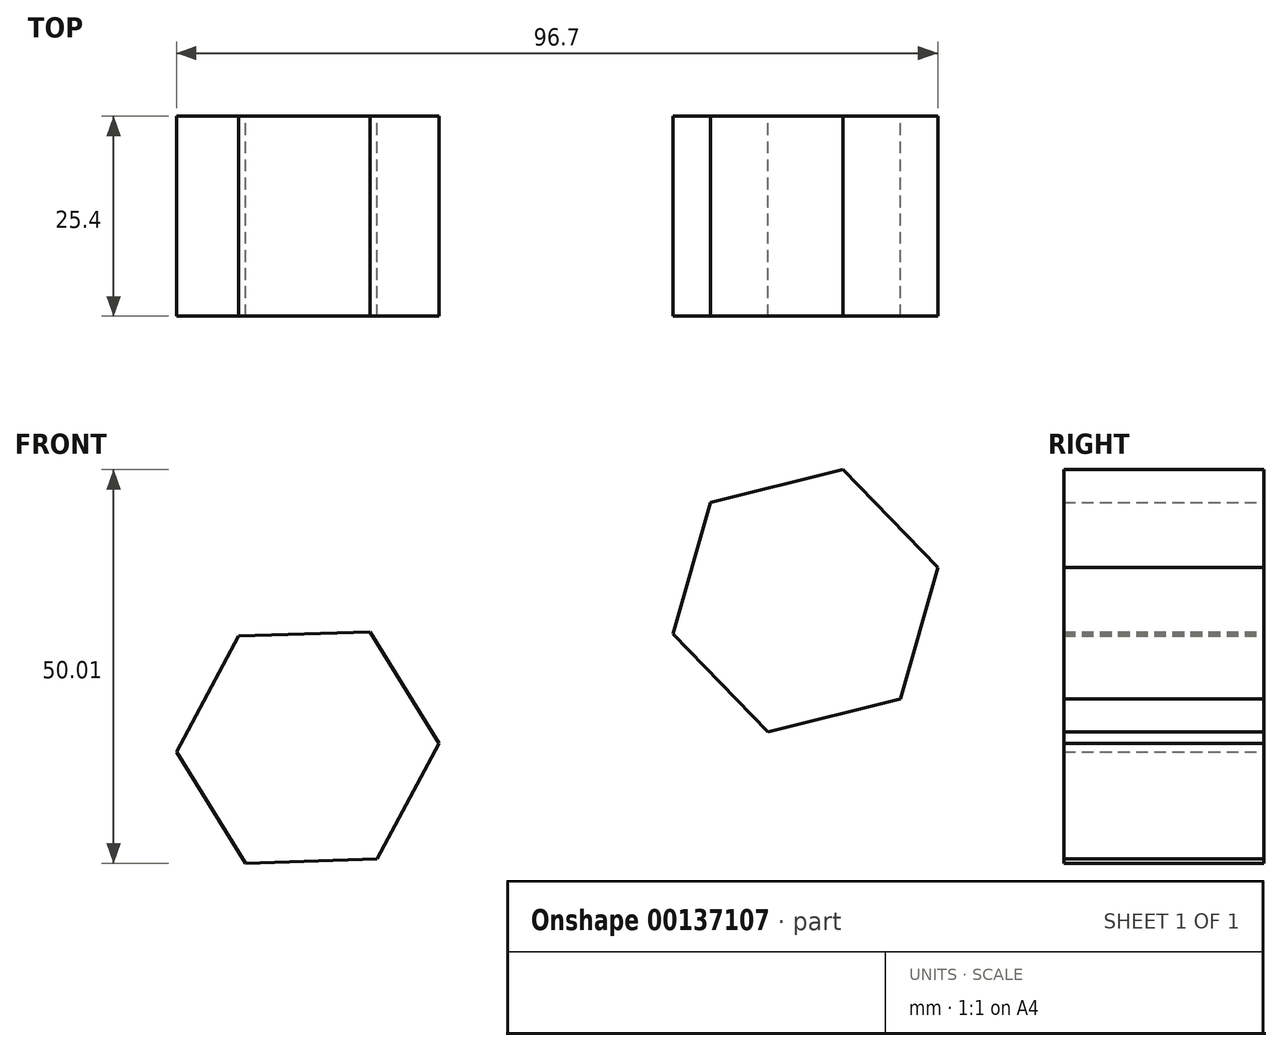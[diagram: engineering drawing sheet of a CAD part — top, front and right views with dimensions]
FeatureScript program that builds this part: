
annotation { "Feature Type Name" : "Feature", "Feature Type Description" : "" }
export const myFeature = defineFeature(function(context is Context, id is Id, definition is map)
    precondition{}
    {
        {
            var Q0;
            Q0=qCreatedBy(makeId("Front.planeOp"),FACE);
            var sketch = newSketch(context, id + "F0", { "sketchPlane" : qUnion([Q0])});
            skCircle(sketch, "E0.cCircle", {"center": v(-30.47, 21.15) * mm, "radius": 14.45 * mm, "construction": true});
            skLineSegment(sketch, "E0.0", {"start": v(-13.8, 21.68) * mm, "end": v(-21.68, 6.97) * mm});
            skLineSegment(sketch, "E0.1", {"start": v(-21.68, 6.97) * mm, "end": v(-38.35, 6.44) * mm});
            skLineSegment(sketch, "E0.2", {"start": v(-38.35, 6.44) * mm, "end": v(-47.15, 20.62) * mm});
            skLineSegment(sketch, "E0.3", {"start": v(-47.15, 20.62) * mm, "end": v(-39.27, 35.32) * mm});
            skLineSegment(sketch, "E0.4", {"start": v(-39.27, 35.32) * mm, "end": v(-22.6, 35.85) * mm});
            skLineSegment(sketch, "E0.5", {"start": v(-22.6, 35.85) * mm, "end": v(-13.8, 21.68) * mm});
            skPoint(sketch, "E0.0.midPoint", {"position": v(-17.74, 14.33) * mm});
            skCircle(sketch, "E1.cCircle", {"center": v(32.75, 39.8) * mm, "radius": 15 * mm, "construction": true});
            skLineSegment(sketch, "E1.0", {"start": v(44.79, 27.34) * mm, "end": v(27.98, 23.14) * mm});
            skLineSegment(sketch, "E1.1", {"start": v(27.98, 23.14) * mm, "end": v(15.94, 35.6) * mm});
            skLineSegment(sketch, "E1.2", {"start": v(15.94, 35.6) * mm, "end": v(20.7, 52.25) * mm});
            skLineSegment(sketch, "E1.3", {"start": v(20.7, 52.25) * mm, "end": v(37.51, 56.45) * mm});
            skLineSegment(sketch, "E1.4", {"start": v(37.51, 56.45) * mm, "end": v(49.55, 44) * mm});
            skLineSegment(sketch, "E1.5", {"start": v(49.55, 44) * mm, "end": v(44.79, 27.34) * mm});
            skPoint(sketch, "E1.0.midPoint", {"position": v(36.39, 25.24) * mm});
            skSolve(sketch);
        }
        {
            var Q0;
            Q0=makeQuery(id+"F0.imprint","IMPRINT",FACE,{"disambiguationData":[TD([[makeQuery(id+"F0.imprint","IMPRINT",EDGE,{"derivedFrom":sQuery(id+"F0.wireOp",EDGE,"E0.0")}),-1.0]])]});
            extrude(context, id + "F1", {"entities" : qUnion([Q0]), "depth" : 25.4 * mm});
        }
        {
            var Q0;
            Q0 = qSketchRegion(id + "F0", true);
            extrude(context, id + "F2", {"entities" : qUnion([Q0]), "depth" : 25.4 * mm});
        }
        {
            var Q0;
            Q0 = qSketchRegion(id + "F0", true);
            extrude(context, id + "F3", {"entities" : qUnion([Q0]), "depth" : 25.4 * mm});
        }
    });
